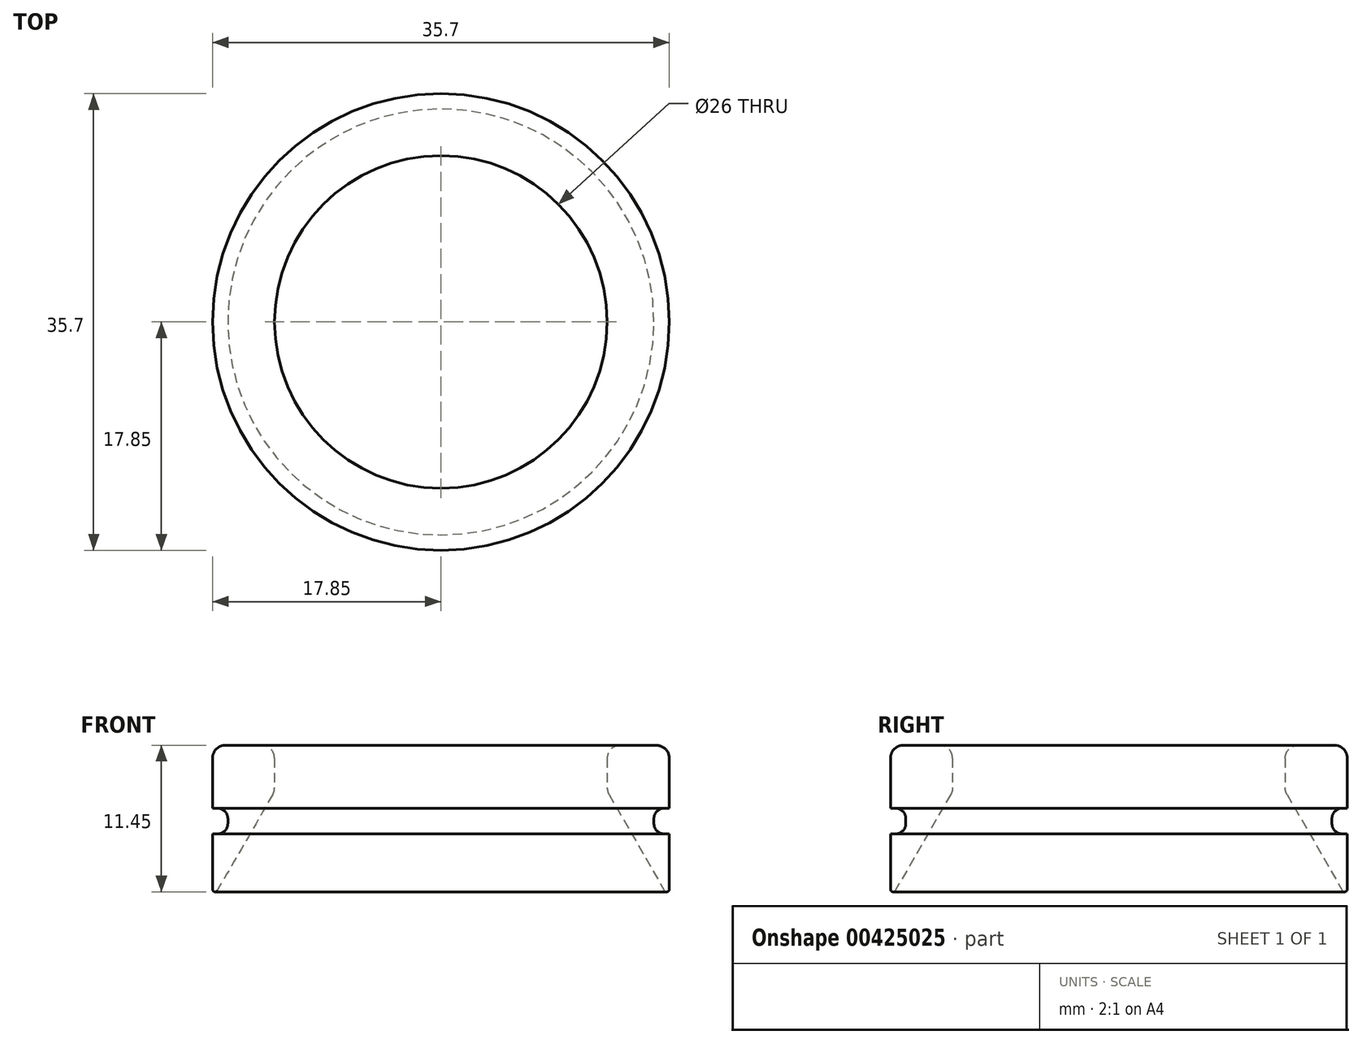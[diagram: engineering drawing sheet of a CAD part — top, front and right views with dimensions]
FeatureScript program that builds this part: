
annotation { "Feature Type Name" : "Feature", "Feature Type Description" : "" }
export const myFeature = defineFeature(function(context is Context, id is Id, definition is map)
    precondition{}
    {
        {
            var Q0;
            Q0=qCreatedBy(makeId("Front.planeOp"),FACE);
            var sketch = newSketch(context, id + "F0", { "sketchPlane" : qUnion([Q0])});
            skLineSegment(sketch, "E0", {"start": v(17.85, 0) * mm, "end": v(17.85, 12) * mm});
            skLineSegment(sketch, "E1", {"start": v(17.85, 0) * mm, "end": v(10.92, 12) * mm});
            skLineSegment(sketch, "E2", {"start": v(17.85, 12) * mm, "end": v(10.92, 12) * mm});
            skLineSegment(sketch, "E3", {"start": v(0, 0) * mm, "end": v(0, 9.48) * mm, "construction": true});
            skLineSegment(sketch, "E4.bottom", {"start": v(17.85, 7.08) * mm, "end": v(16.65, 7.08) * mm});
            skLineSegment(sketch, "E4.top", {"start": v(17.85, 5.08) * mm, "end": v(16.65, 5.08) * mm});
            skLineSegment(sketch, "E4.left", {"start": v(17.85, 7.08) * mm, "end": v(17.85, 5.08) * mm});
            skLineSegment(sketch, "E4.right", {"start": v(16.65, 7.08) * mm, "end": v(16.65, 5.08) * mm});
            skLineSegment(sketch, "E5", {"start": v(13, 12) * mm, "end": v(13, 8.4) * mm});
            skSolve(sketch);
        }
        {
            var Q0;
            {var subQ7=sQuery(id+"F0.wireOp",EDGE,"E4.bottom");Q0=makeQuery(id+"F0.imprint","IMPRINT",FACE,{"disambiguationData":[TD([[makeQuery(id+"F0.imprint","IMPRINT",EDGE,{"derivedFrom":subQ7}),-1.0]])]});}
            var Q1;
            Q1=sQuery(id+"F0.wireOp",EDGE,"E3");
            revolve(context, id + "F1", {"entities" : qUnion([Q0]), "axis" : qUnion([Q1]), "revolveType" : RevolveType.FULL});
        }
        {
            var Q0;
            Q0=makeQuery(id+"F1.opRevolve","SWEPT_FACE",FACE,{"disambiguationData":[OSD([sQuery(id+"F0.wireOp",EDGE,"E5")])]});
            var Q1;
            Q1=makeQuery(id+"F1.opRevolve","SWEPT_EDGE",EDGE,{"disambiguationData":[OSD([sQuery(id+"F0.wireOp",EDGE,"E0"),sQuery(id+"F0.wireOp",EDGE,"E2")])]});
            fillet(context, id + "F2", {"entities" : qUnion([Q0, Q1]), "radius" : 1 * mm, "tangentPropagation" : true, "allowEdgeOverflow" : false});
        }
        {
            var Q0;
            Q0=makeQuery(id+"F1.opRevolve","SWEPT_EDGE",EDGE,{"disambiguationData":[OSD([sQuery(id+"F0.wireOp",EDGE,"E4.bottom"),sQuery(id+"F0.wireOp",EDGE,"E4.right")])]});
            var Q1;
            Q1=makeQuery(id+"F1.opRevolve","SWEPT_EDGE",EDGE,{"disambiguationData":[OSD([sQuery(id+"F0.wireOp",EDGE,"E4.top"),sQuery(id+"F0.wireOp",EDGE,"E4.right")])]});
            fillet(context, id + "F3", {"entities" : qUnion([Q0, Q1]), "radius" : .8 * mm, "tangentPropagation" : true, "allowEdgeOverflow" : false});
        }
        {
            var Q0;
            Q0=makeQuery(id+"F1.opRevolve","SWEPT_EDGE",EDGE,{"disambiguationData":[OSD([sQuery(id+"F0.wireOp",EDGE,"E0"),sQuery(id+"F0.wireOp",EDGE,"E1")])]});
            fillet(context, id + "F4", {"entities" : qUnion([Q0]), "radius" : .2 * mm, "tangentPropagation" : true, "allowEdgeOverflow" : false});
        }
    });
